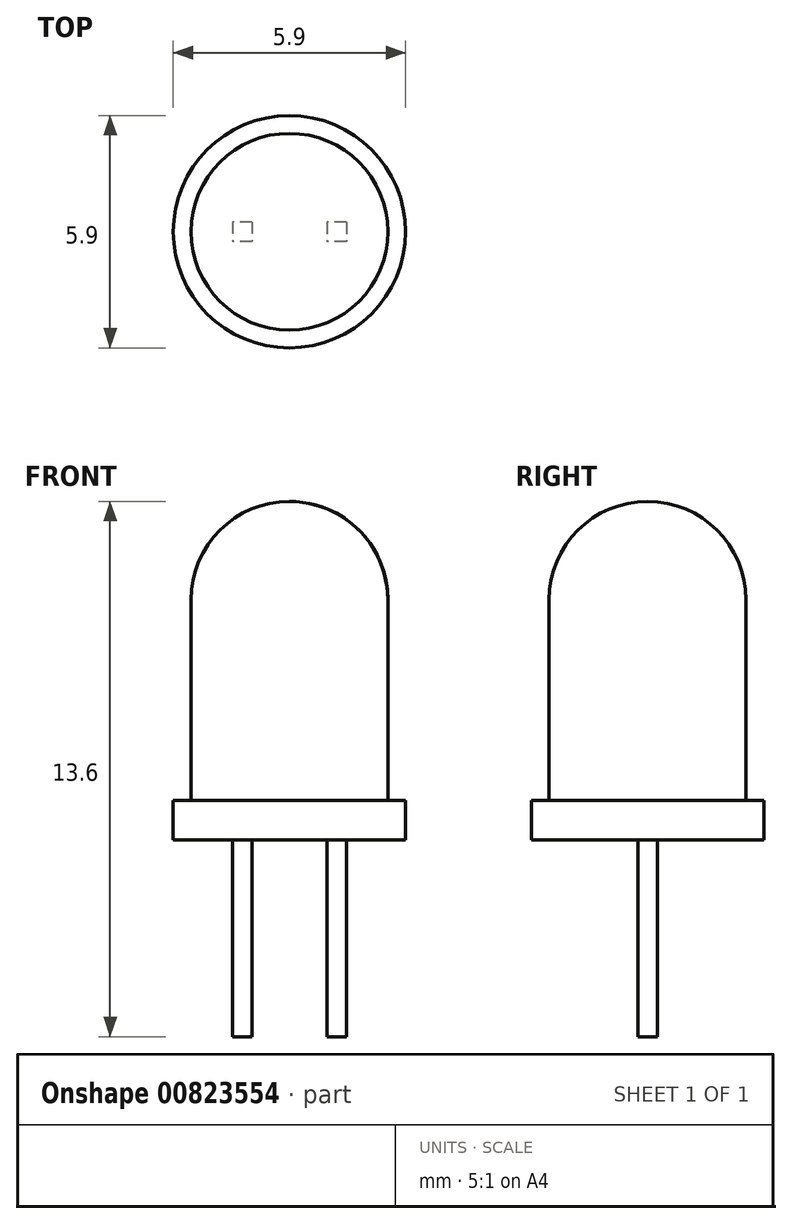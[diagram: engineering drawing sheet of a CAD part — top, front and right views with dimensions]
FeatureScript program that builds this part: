
annotation { "Feature Type Name" : "Feature", "Feature Type Description" : "" }
export const myFeature = defineFeature(function(context is Context, id is Id, definition is map)
    precondition{}
    {
        {
            var Q0;
            Q0=qCreatedBy(makeId("Top.planeOp"),FACE);
            var sketch = newSketch(context, id + "F0", { "sketchPlane" : qUnion([Q0])});
            skCircle(sketch, "E0", {"center": v(0, 0) * mm, "radius": 2.5 * mm});
            skCircle(sketch, "E1", {"center": v(0, 0) * mm, "radius": 2.95 * mm});
            skSolve(sketch);
        }
        {
            var Q0;
            Q0=makeQuery(id+"F0.imprint","IMPRINT",FACE,{"disambiguationData":[TD([[makeQuery(id+"F0.imprint","IMPRINT",EDGE,{"derivedFrom":sQuery(id+"F0.wireOp",EDGE,"E0")}),1.0]])]});
            extrude(context, id + "F1", {"entities" : qUnion([Q0]), "depth" : 8.6 * mm, "offsetDistance" : 25 * mm});
        }
        {
            var Q0;
            Q0=makeQuery(id+"F0.imprint","IMPRINT",FACE,{"disambiguationData":[TD([[makeQuery(id+"F0.imprint","IMPRINT",EDGE,{"derivedFrom":sQuery(id+"F0.wireOp",EDGE,"E0")}),-1.0]])]});
            extrude(context, id + "F2", {"entities" : qUnion([Q0]), "operationType" : NewBodyOperationType.ADD, "depth" : 1 * mm, "offsetDistance" : 25 * mm});
        }
        {
            var Q0;
            Q0=makeQuery(id+"F1.opExtrude","CAP_EDGE",EDGE,{"disambiguationData":[OSD([sQuery(id+"F0.wireOp",EDGE,"E0")])],"isStart":false});
            fillet(context, id + "F3", {"entities" : qUnion([Q0]), "radius" : 2.5 * mm, "tangentPropagation" : true, "allowEdgeOverflow" : false});
        }
        {
            var Q0;
            Q0=makeQuery(id+"F0.imprint","IMPRINT",FACE,{"disambiguationData":[TD([[makeQuery(id+"F0.imprint","IMPRINT",EDGE,{"derivedFrom":sQuery(id+"F0.wireOp",EDGE,"E0")}),1.0]])]});
            var sketch = newSketch(context, id + "F4", { "sketchPlane" : qUnion([Q0])});
            skLineSegment(sketch, "E2.bottom", {"start": v(1.45, 0.25) * mm, "end": v(0.95, 0.25) * mm});
            skLineSegment(sketch, "E2.top", {"start": v(1.45, -0.25) * mm, "end": v(0.95, -0.25) * mm});
            skLineSegment(sketch, "E2.left", {"start": v(1.45, 0.25) * mm, "end": v(1.45, -0.25) * mm});
            skLineSegment(sketch, "E2.right", {"start": v(0.95, 0.25) * mm, "end": v(0.95, -0.25) * mm});
            skPoint(sketch, "E2.middle", {"position": v(1.2, 0) * mm});
            skLineSegment(sketch, "E3.bottom", {"start": v(-0.95, 0.25) * mm, "end": v(-1.45, 0.25) * mm});
            skLineSegment(sketch, "E3.top", {"start": v(-0.95, -0.25) * mm, "end": v(-1.45, -0.25) * mm});
            skLineSegment(sketch, "E3.left", {"start": v(-0.95, 0.25) * mm, "end": v(-0.95, -0.25) * mm});
            skLineSegment(sketch, "E3.right", {"start": v(-1.45, 0.25) * mm, "end": v(-1.45, -0.25) * mm});
            skPoint(sketch, "E3.middle", {"position": v(-1.2, 0) * mm});
            skLineSegment(sketch, "E4", {"start": v(-0.95, 0) * mm, "end": v(0.95, 0) * mm, "construction": true});
            skSolve(sketch);
        }
        {
            var Q0;
            Q0 = qSketchRegion(id + "F4", true);
            extrude(context, id + "F5", {"entities" : qUnion([Q0]), "oppositeDirection" : true, "depth" : 5 * mm, "offsetDistance" : 25 * mm});
        }
    });
